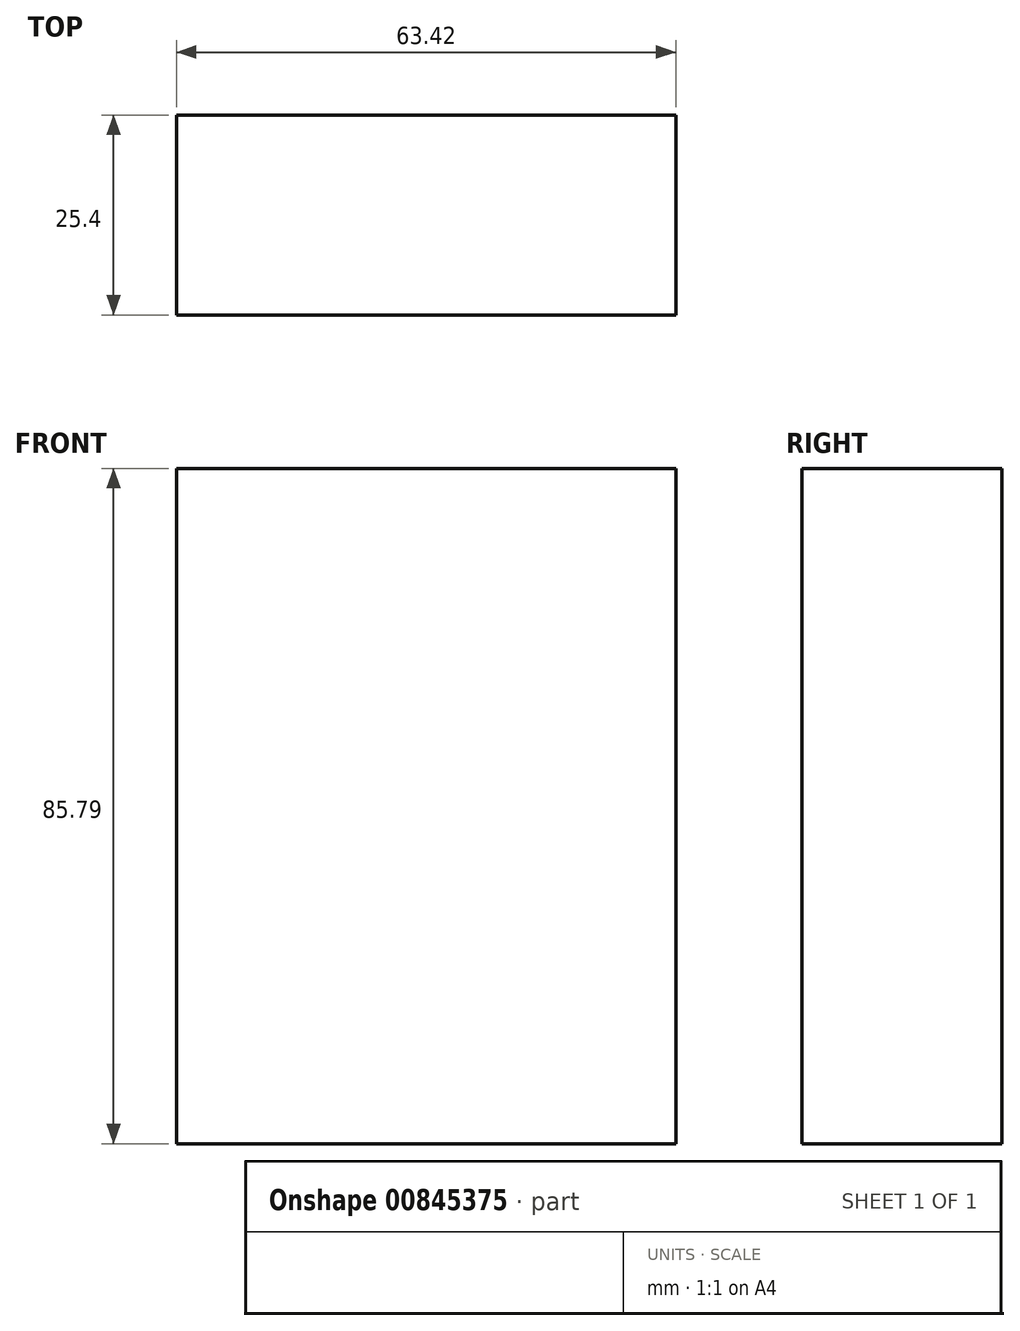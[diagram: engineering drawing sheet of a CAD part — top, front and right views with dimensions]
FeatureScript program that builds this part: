
annotation { "Feature Type Name" : "Feature", "Feature Type Description" : "" }
export const myFeature = defineFeature(function(context is Context, id is Id, definition is map)
    precondition{}
    {
        {
            var Q0;
            Q0=qCreatedBy(makeId("Front.planeOp"),FACE);
            var sketch = newSketch(context, id + "F0", { "sketchPlane" : qUnion([Q0])});
            skLineSegment(sketch, "E0.bottom", {"start": v(-146.16, 34.62) * mm, "end": v(-209.58, 34.62) * mm});
            skLineSegment(sketch, "E0.top", {"start": v(-146.16, -51.17) * mm, "end": v(-209.58, -51.17) * mm});
            skLineSegment(sketch, "E0.left", {"start": v(-146.16, 34.62) * mm, "end": v(-146.16, -51.17) * mm});
            skLineSegment(sketch, "E0.right", {"start": v(-209.58, 34.62) * mm, "end": v(-209.58, -51.17) * mm});
            skSolve(sketch);
        }
        {
            var Q0;
            Q0 = qSketchRegion(id + "F0", true);
            extrude(context, id + "F1", {"entities" : qUnion([Q0]), "depth" : 25.4 * mm, "offsetDistance" : 25.4 * mm});
        }
    });
